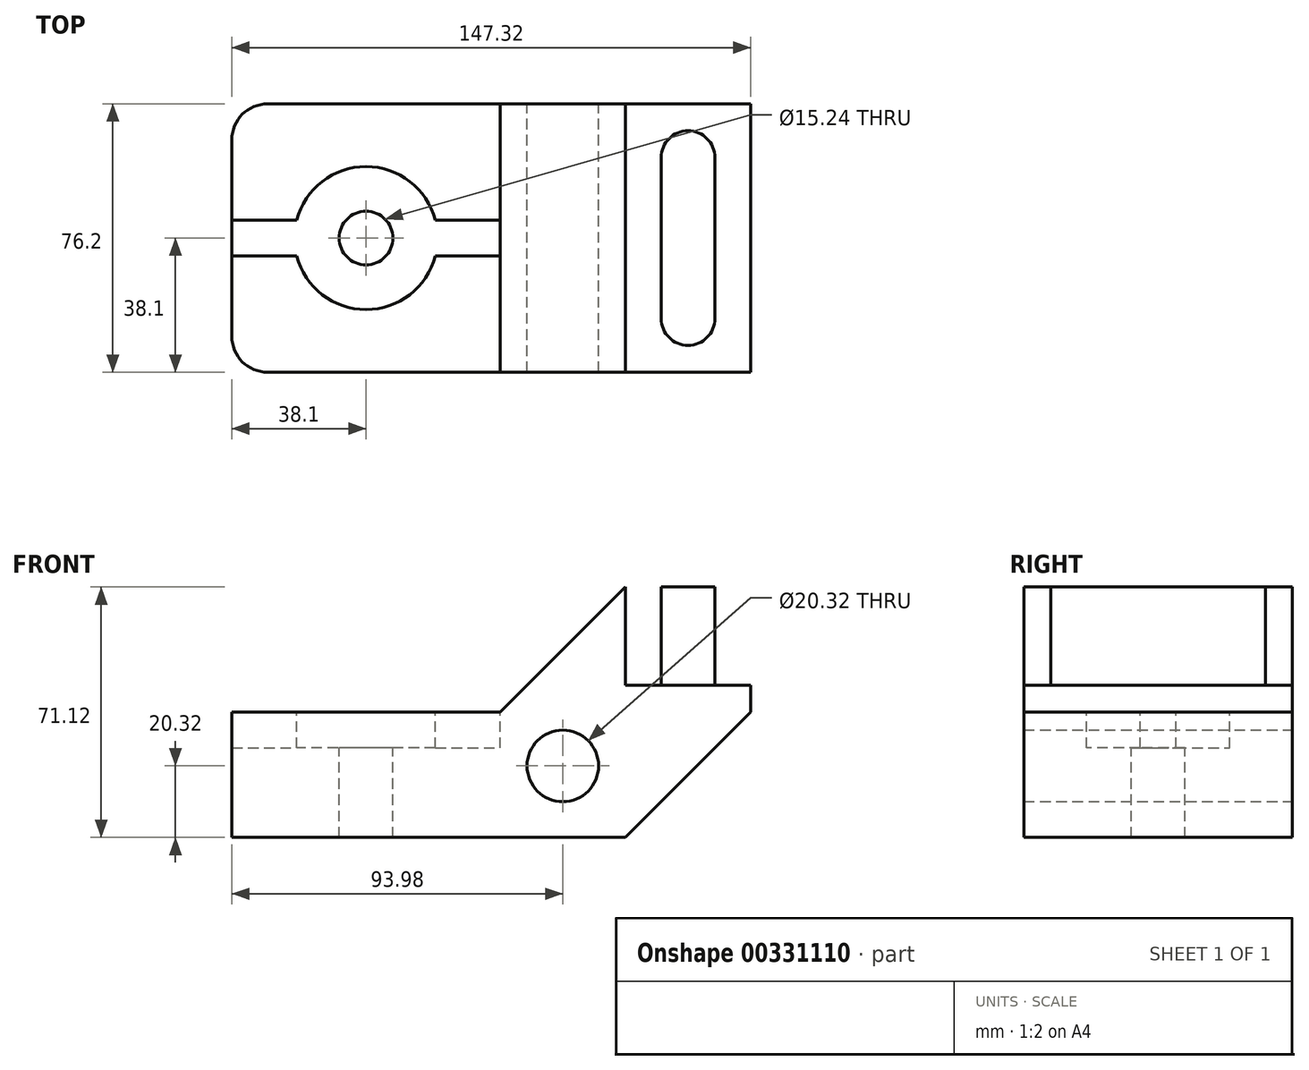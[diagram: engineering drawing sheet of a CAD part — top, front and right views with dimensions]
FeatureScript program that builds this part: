
annotation { "Feature Type Name" : "Feature", "Feature Type Description" : "" }
export const myFeature = defineFeature(function(context is Context, id is Id, definition is map)
    precondition{}
    {
        {
            var Q0;
            Q0=qCreatedBy(makeId("Front.planeOp"),FACE);
            var sketch = newSketch(context, id + "F0", { "sketchPlane" : qUnion([Q0])});
            skLineSegment(sketch, "E0", {"start": v(-111.76, 0) * mm, "end": v(0, 0) * mm});
            skLineSegment(sketch, "E1", {"start": v(0, 0) * mm, "end": v(35.56, 35.56) * mm});
            skLineSegment(sketch, "E2", {"start": v(35.56, 35.56) * mm, "end": v(35.56, 71.12) * mm});
            skLineSegment(sketch, "E3", {"start": v(35.56, 71.12) * mm, "end": v(0, 71.12) * mm});
            skLineSegment(sketch, "E4", {"start": v(0, 71.12) * mm, "end": v(-35.56, 35.56) * mm});
            skLineSegment(sketch, "E5", {"start": v(-35.56, 35.56) * mm, "end": v(-111.76, 35.56) * mm});
            skLineSegment(sketch, "E6", {"start": v(-111.76, 35.56) * mm, "end": v(-111.76, 0) * mm});
            skCircle(sketch, "E7", {"center": v(-17.78, 20.32) * mm, "radius": 10.16 * mm});
            skSolve(sketch);
        }
        {
            var Q0;
            Q0 = qSketchRegion(id + "F0", true);
            extrude(context, id + "F1", {"entities" : qUnion([Q0]), "endBound" : BoundingType.SYMMETRIC, "depth" : 76.2 * mm});
        }
        {
            var Q0;
            Q0=makeQuery(id+"F1.opExtrude","CAP_EDGE",EDGE,{"disambiguationData":[OSD([sQuery(id+"F0.wireOp",EDGE,"E6")])],"isStart":false});
            var Q1;
            Q1=makeQuery(id+"F1.opExtrude","CAP_EDGE",EDGE,{"disambiguationData":[OSD([sQuery(id+"F0.wireOp",EDGE,"E6")])],"isStart":true});
            fillet(context, id + "F2", {"entities" : qUnion([Q0, Q1]), "radius" : 10.16 * mm, "tangentPropagation" : true, "allowEdgeOverflow" : false});
        }
        {
            var Q0;
            Q0=makeQuery(id+"F1.opExtrude","SWEPT_FACE",FACE,{"disambiguationData":[OSD([sQuery(id+"F0.wireOp",EDGE,"E3")])]});
            var sketch = newSketch(context, id + "F3", { "sketchPlane" : qUnion([Q0])});
            skPoint(sketch, "E8", {"position": v(17.78, 22.86) * mm});
            skPoint(sketch, "E9", {"position": v(17.78, -22.86) * mm});
            skLineSegment(sketch, "E10", {"start": v(17.78, -22.86) * mm, "end": v(17.78, 22.86) * mm});
            skArc(sketch, "E11.0.startCap", {"start": v(25.4, -22.86) * mm, "mid": v(17.78, -30.48) * mm, "end": v(10.16, -22.86) * mm});
            skArc(sketch, "E11.0.endCap", {"start": v(10.16, 22.86) * mm, "mid": v(17.78, 30.48) * mm, "end": v(25.4, 22.86) * mm});
            skLineSegment(sketch, "E11.0.left", {"start": v(10.16, -22.86) * mm, "end": v(10.16, 22.86) * mm});
            skLineSegment(sketch, "E11.0.right", {"start": v(25.4, -22.86) * mm, "end": v(25.4, 22.86) * mm});
            skSolve(sketch);
        }
        {
            var Q0;
            Q0=makeQuery(id+"F3.imprint","IMPRINT",FACE,{"disambiguationData":[TD([[makeQuery(id+"F3.imprint","IMPRINT",EDGE,{"derivedFrom":sQuery(id+"F3.wireOp",EDGE,"E11.0.startCap")}),-1.0]])]});
            extrude(context, id + "F4", {"entities" : qUnion([Q0]), "operationType" : NewBodyOperationType.REMOVE, "oppositeDirection" : true, "depth" : 27.94 * mm});
        }
        {
            var Q0;
            Q0=makeQuery(id+"F1.opExtrude","SWEPT_FACE",FACE,{"disambiguationData":[OSD([sQuery(id+"F0.wireOp",EDGE,"E5")])]});
            var sketch = newSketch(context, id + "F5", { "sketchPlane" : qUnion([Q0])});
            skLineSegment(sketch, "E12", {"start": v(-73.66, 38.1) * mm, "end": v(-73.66, -38.1) * mm, "construction": true});
            skPoint(sketch, "E13", {"position": v(-73.66, 0) * mm});
            skLineSegment(sketch, "E14", {"start": v(-111.76, 0) * mm, "end": v(-35.56, 0) * mm, "construction": true});
            skLineSegment(sketch, "E15", {"start": v(-111.76, -5.08) * mm, "end": v(-35.56, -5.08) * mm});
            skLineSegment(sketch, "E16.MirrorCS", {"start": v(-111.76, 5.08) * mm, "end": v(-35.56, 5.08) * mm});
            skLineSegment(sketch, "E17", {"start": v(-111.76, -5.08) * mm, "end": v(-111.76, 5.08) * mm});
            skLineSegment(sketch, "E18", {"start": v(-35.56, -5.08) * mm, "end": v(-35.56, 5.08) * mm});
            skCircle(sketch, "E19", {"center": v(-73.66, 0) * mm, "radius": 20.32 * mm});
            skSolve(sketch);
        }
        {
            var Q0;
            {var subQ0=sQuery(id+"F5.wireOp",EDGE,"E18");Q0=makeQuery(id+"F5.imprint","IMPRINT",FACE,{"disambiguationData":[TD([[makeQuery(id+"F5.imprint","IMPRINT",EDGE,{"derivedFrom":subQ0}),1.0]])]});}
            var Q1;
            {var subQ0=sQuery(id+"F5.wireOp",EDGE,"E19");var subQ1=sQuery(id+"F5.wireOp",EDGE,"E15");var subQ2=makeQuery(id+"F5.imprint","INTERSECT",VERTEX,{"disambiguationData":[OD(0.0)],"derivedFrom":[subQ1,subQ0]});Q1=makeQuery(id+"F5.imprint","IMPRINT",FACE,{"disambiguationData":[TD([[makeQuery(id+"F5.imprint","IMPRINT",EDGE,{"disambiguationData":[TD([[subQ2,-1.0]])],"derivedFrom":subQ1}),-1.0]])]});}
            var Q2;
            {var subQ0=sQuery(id+"F5.wireOp",EDGE,"E19");var subQ1=sQuery(id+"F5.wireOp",EDGE,"E15");var subQ2=makeQuery(id+"F5.imprint","INTERSECT",VERTEX,{"disambiguationData":[OD(0.0)],"derivedFrom":[subQ1,subQ0]});Q2=makeQuery(id+"F5.imprint","IMPRINT",FACE,{"disambiguationData":[TD([[makeQuery(id+"F5.imprint","IMPRINT",EDGE,{"disambiguationData":[TD([[subQ2,-1.0]])],"derivedFrom":subQ1}),1.0]])]});}
            var Q3;
            {var subQ0=sQuery(id+"F5.wireOp",EDGE,"E19");var subQ1=sQuery(id+"F5.wireOp",EDGE,"E16.MirrorCS");var subQ2=makeQuery(id+"F5.imprint","INTERSECT",VERTEX,{"disambiguationData":[OD(0.0)],"derivedFrom":[subQ1,subQ0]});Q3=makeQuery(id+"F5.imprint","IMPRINT",FACE,{"disambiguationData":[TD([[makeQuery(id+"F5.imprint","IMPRINT",EDGE,{"disambiguationData":[TD([[subQ2,-1.0]])],"derivedFrom":subQ1}),1.0]])]});}
            var Q4;
            {var subQ0=sQuery(id+"F5.wireOp",EDGE,"E17");Q4=makeQuery(id+"F5.imprint","IMPRINT",FACE,{"disambiguationData":[TD([[makeQuery(id+"F5.imprint","IMPRINT",EDGE,{"derivedFrom":subQ0}),-1.0]])]});}
            extrude(context, id + "F6", {"entities" : qUnion([Q0, Q1, Q2, Q3, Q4]), "operationType" : NewBodyOperationType.REMOVE, "oppositeDirection" : true, "depth" : 10.16 * mm});
        }
        {
            var Q0;
            Q0=sQuery(id+"F5.wireOp",VERTEX,"E13");
            var Q1;
            Q1=makeQuery(id+"F1.opExtrude","SWEPT_BODY",BODY,{"disambiguationData":[OSD([sQuery(id+"F0.wireOp",EDGE,"E0"),sQuery(id+"F0.wireOp",EDGE,"E1"),sQuery(id+"F0.wireOp",EDGE,"E2"),sQuery(id+"F0.wireOp",EDGE,"E3"),sQuery(id+"F0.wireOp",EDGE,"E4"),sQuery(id+"F0.wireOp",EDGE,"E5"),sQuery(id+"F0.wireOp",EDGE,"E6"),sQuery(id+"F0.wireOp",EDGE,"E7")])]});
            hole(context, id + "F7", {"style" : HoleStyle.SIMPLE, "endStyle" : HoleEndStyle.THROUGH, "holeDiameter" : 15.24 * mm, "tappedDepth" : 12.7 * mm, "tapClearance" : 3, "locations" : qUnion([Q0]), "scope" : qUnion([Q1])});
        }
    });
